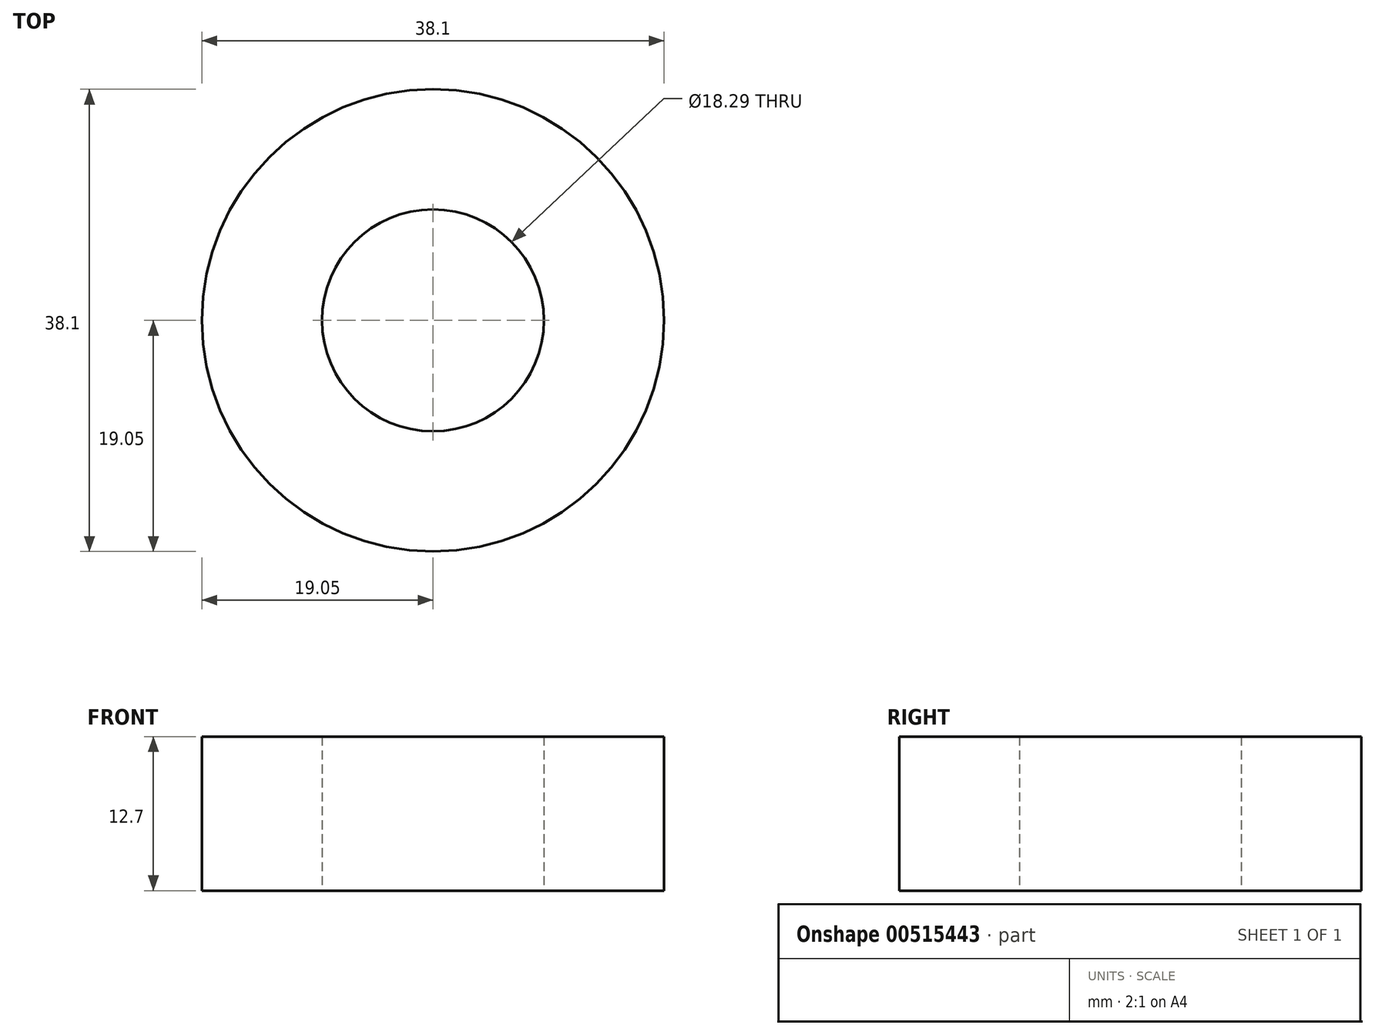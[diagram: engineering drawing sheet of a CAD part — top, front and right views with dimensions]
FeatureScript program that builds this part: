
annotation { "Feature Type Name" : "Feature", "Feature Type Description" : "" }
export const myFeature = defineFeature(function(context is Context, id is Id, definition is map)
    precondition{}
    {
        {
            var Q0;
            Q0=qCreatedBy(makeId("Top.planeOp"),FACE);
            var sketch = newSketch(context, id + "F0", { "sketchPlane" : qUnion([Q0])});
            skCircle(sketch, "E0", {"center": v(0, 0) * mm, "radius": 19.05 * mm});
            skCircle(sketch, "E1", {"center": v(0, 0) * mm, "radius": 9.14 * mm});
            skSolve(sketch);
        }
        {
            var Q0;
            Q0=makeQuery(id+"F0.imprint","IMPRINT",FACE,{"disambiguationData":[TD([[makeQuery(id+"F0.imprint","IMPRINT",EDGE,{"derivedFrom":sQuery(id+"F0.wireOp",EDGE,"E0")}),1.0]])]});
            extrude(context, id + "F1", {"entities" : qUnion([Q0]), "depth" : 12.7 * mm, "offsetDistance" : 25.4 * mm});
        }
    });
